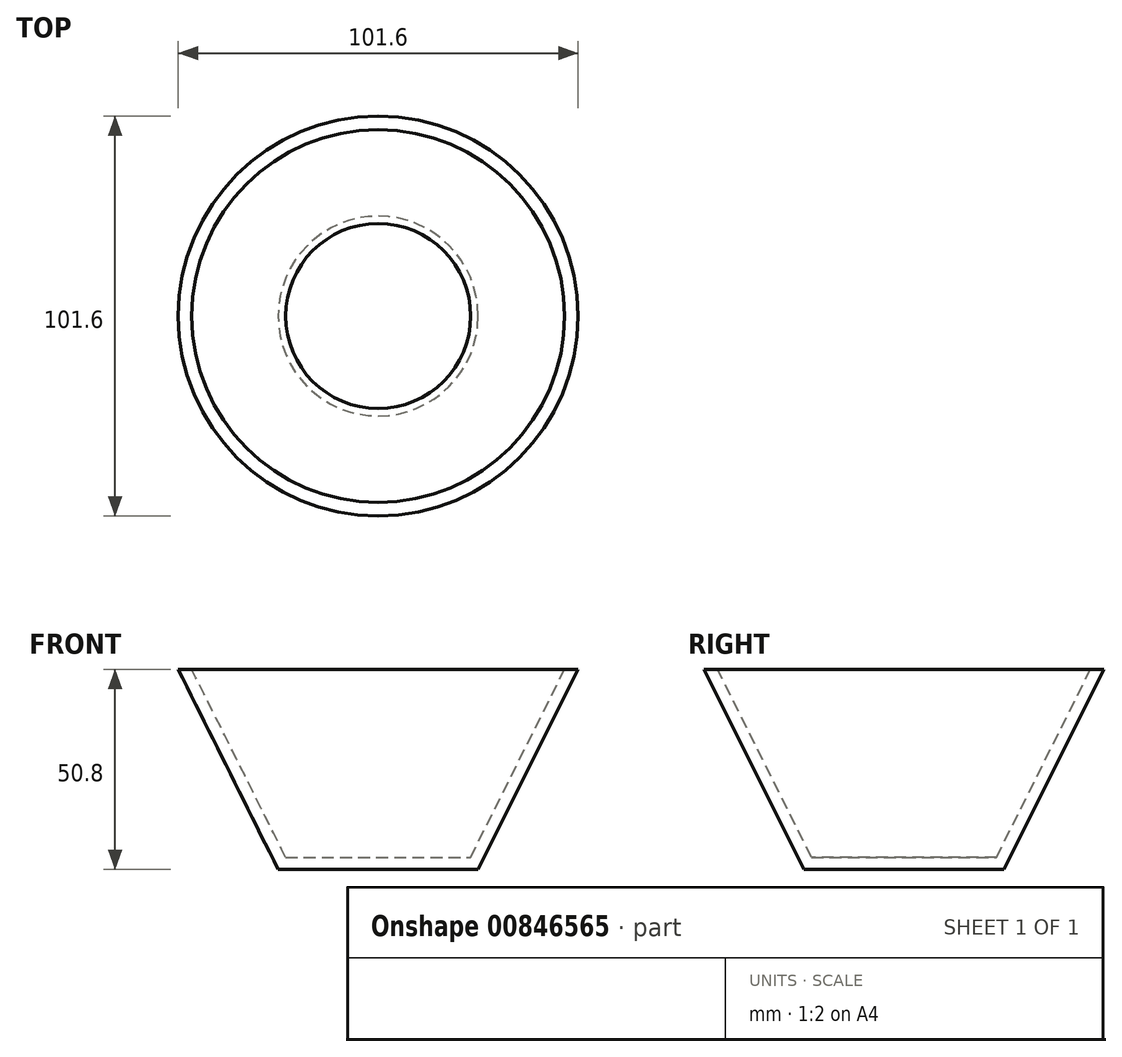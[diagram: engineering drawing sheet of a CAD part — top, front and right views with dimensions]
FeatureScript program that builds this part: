
annotation { "Feature Type Name" : "Feature", "Feature Type Description" : "" }
export const myFeature = defineFeature(function(context is Context, id is Id, definition is map)
    precondition{}
    {
        {
            var Q0;
            Q0=qCreatedBy(makeId("Front.planeOp"),FACE);
            var sketch = newSketch(context, id + "F0", { "sketchPlane" : qUnion([Q0])});
            skLineSegment(sketch, "E0", {"start": v(0, 0) * mm, "end": v(0, 50.8) * mm, "construction": true});
            skLineSegment(sketch, "E1", {"start": v(0, 0) * mm, "end": v(25.4, 0) * mm});
            skLineSegment(sketch, "E2", {"start": v(25.4, 0) * mm, "end": v(50.8, 50.8) * mm});
            skLineSegment(sketch, "E3", {"start": v(0, 0) * mm, "end": v(-25.4, 0) * mm});
            skLineSegment(sketch, "E4", {"start": v(0, 50.8) * mm, "end": v(-25.4, 50.8) * mm});
            skLineSegment(sketch, "E5.0", {"start": v(23.5, 3.07) * mm, "end": v(47.36, 50.8) * mm});
            skLineSegment(sketch, "E5.1", {"start": v(0, 3.07) * mm, "end": v(23.5, 3.07) * mm});
            skPoint(sketch, "E6", {"position": v(47.36, 50.8) * mm});
            skLineSegment(sketch, "E7", {"start": v(47.36, 50.8) * mm, "end": v(50.8, 50.8) * mm});
            skLineSegment(sketch, "E8", {"start": v(0, 3.07) * mm, "end": v(0, 0) * mm});
            skSolve(sketch);
        }
        {
            var Q0;
            Q0=makeQuery(id+"F0.imprint","IMPRINT",FACE,{"disambiguationData":[TD([[makeQuery(id+"F0.imprint","IMPRINT",EDGE,{"derivedFrom":sQuery(id+"F0.wireOp",EDGE,"E1")}),1.0]])]});
            var Q1;
            Q1=sQuery(id+"F0.wireOp",EDGE,"E0");
            revolve(context, id + "F1", {"surfaceOperationType" : NewSurfaceOperationType.NEW, "entities" : qUnion([Q0]), "axis" : qUnion([Q1]), "revolveType" : RevolveType.FULL});
        }
    });
